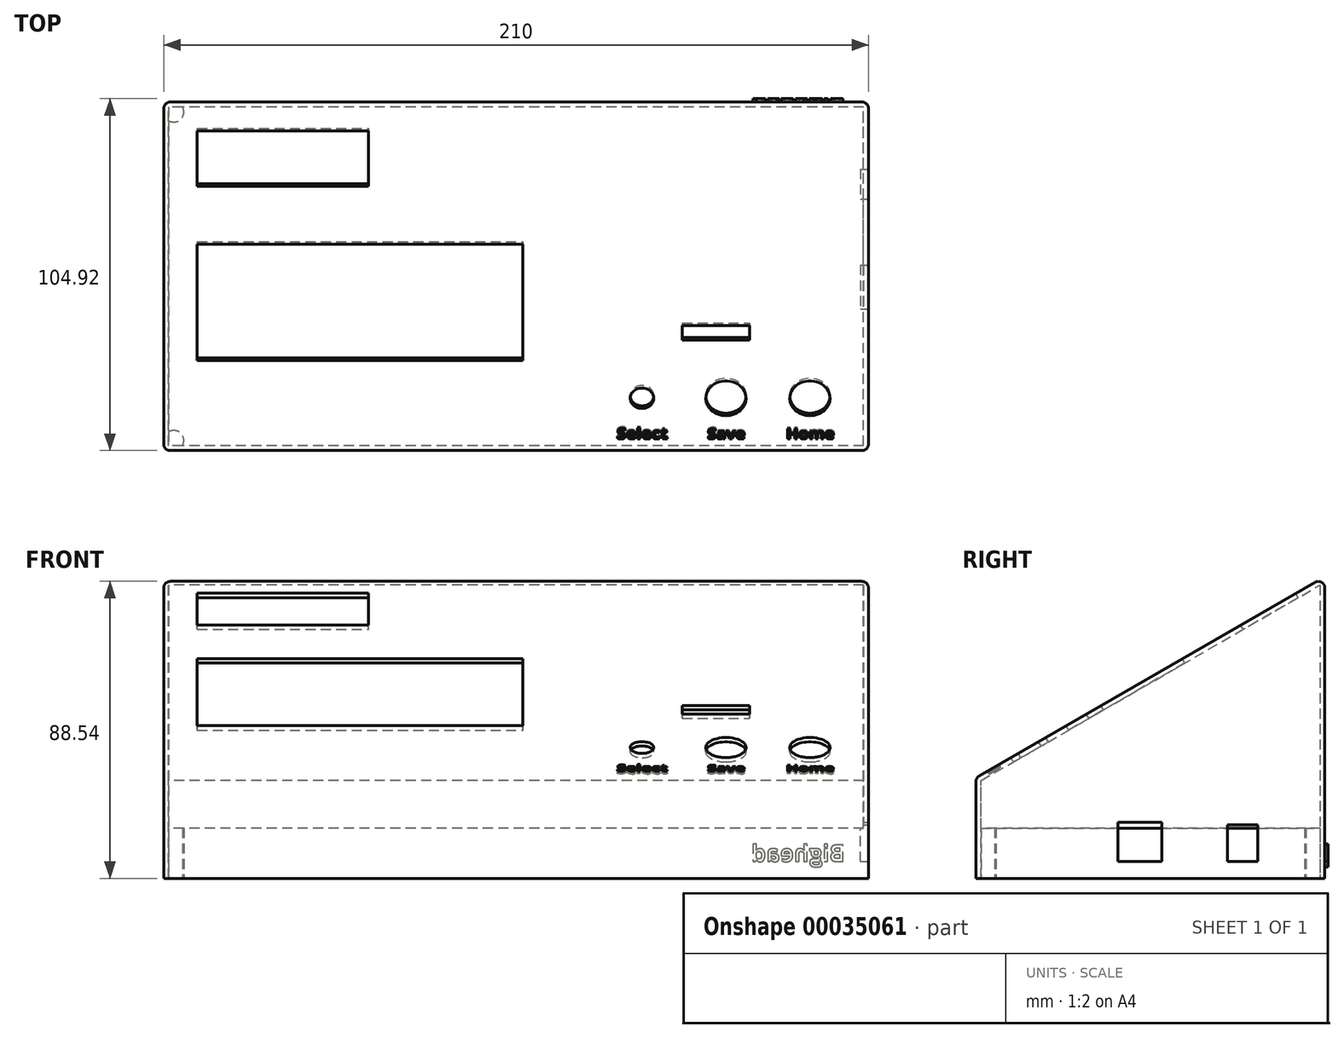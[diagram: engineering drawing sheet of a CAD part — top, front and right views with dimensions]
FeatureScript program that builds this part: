
annotation { "Feature Type Name" : "Feature", "Feature Type Description" : "" }
export const myFeature = defineFeature(function(context is Context, id is Id, definition is map)
    precondition{}
    {
        {
            var Q0;
            Q0=qCreatedBy(makeId("Right.planeOp"),FACE);
            var sketch = newSketch(context, id + "F0", { "sketchPlane" : qUnion([Q0])});
            skLineSegment(sketch, "E0", {"start": v(0, 0) * mm, "end": v(0, 30) * mm});
            skLineSegment(sketch, "E1", {"start": v(0, 30) * mm, "end": v(103.92, 90) * mm});
            skLineSegment(sketch, "E2", {"start": v(103.92, 90) * mm, "end": v(103.92, 0) * mm});
            skLineSegment(sketch, "E3", {"start": v(103.92, 0) * mm, "end": v(0, 0) * mm});
            skSolve(sketch);
        }
        {
            var Q0;
            Q0 = qSketchRegion(id + "F0", true);
            extrude(context, id + "F1", {"entities" : qUnion([Q0]), "depth" : 210 * mm});
        }
        {
            var Q0;
            Q0=makeQuery(id+"F1.opExtrude","SWEPT_FACE",FACE,{"disambiguationData":[OSD([sQuery(id+"F0.wireOp",EDGE,"E3")])]});
            shell(context, id + "F2", {"entities" : qUnion([Q0]), "thickness" : 1.5 * mm});
        }
        {
            var Q0;
            Q0=makeQuery(id+"F1.opExtrude","SWEPT_FACE",FACE,{"disambiguationData":[OSD([sQuery(id+"F0.wireOp",EDGE,"E1")])]});
            var sketch = newSketch(context, id + "F3", { "sketchPlane" : qUnion([Q0])});
            skLineSegment(sketch, "E4.bottom", {"start": v(10, 125) * mm, "end": v(61, 125) * mm});
            skLineSegment(sketch, "E4.top", {"start": v(10, 106) * mm, "end": v(61, 106) * mm});
            skLineSegment(sketch, "E4.left", {"start": v(10, 125) * mm, "end": v(10, 106) * mm});
            skLineSegment(sketch, "E4.right", {"start": v(61, 125) * mm, "end": v(61, 106) * mm});
            skLineSegment(sketch, "E5.bottom", {"start": v(10, 86) * mm, "end": v(107, 86) * mm});
            skLineSegment(sketch, "E5.top", {"start": v(10, 46) * mm, "end": v(107, 46) * mm});
            skLineSegment(sketch, "E5.left", {"start": v(10, 86) * mm, "end": v(10, 46) * mm});
            skLineSegment(sketch, "E5.right", {"start": v(107, 86) * mm, "end": v(107, 46) * mm});
            skCircle(sketch, "E6", {"center": v(142.5, 33) * mm, "radius": 3.5 * mm});
            skCircle(sketch, "E7", {"center": v(167.5, 33) * mm, "radius": 6 * mm});
            skCircle(sketch, "E8", {"center": v(192.5, 33) * mm, "radius": 6 * mm});
            skCircle(sketch, "E9", {"center": v(192.5, 33) * mm, "radius": 8.75 * mm, "construction": true});
            skSolve(sketch);
        }
        {
            var Q0;
            Q0 = qSketchRegion(id + "F3", true);
            extrude(context, id + "F4", {"entities" : qUnion([Q0]), "operationType" : NewBodyOperationType.REMOVE, "oppositeDirection" : true, "depth" : 2.5 * mm});
        }
        {
            var Q0;
            Q0=makeQuery(id+"F3.imprint","IMPRINT",FACE,{"disambiguationData":[TD([[makeQuery(id+"F3.imprint","IMPRINT",EDGE,{"derivedFrom":sQuery(id+"F3.wireOp",EDGE,"E4.bottom")}),1.0]])]});
            var sketch = newSketch(context, id + "F5", { "sketchPlane" : qUnion([Q0])});
            skLineSegment(sketch, "E10.bottom", {"start": v(129, 125) * mm, "end": v(200, 125) * mm, "construction": true});
            skLineSegment(sketch, "E10.top", {"start": v(129, 48) * mm, "end": v(200, 48) * mm, "construction": true});
            skLineSegment(sketch, "E10.left", {"start": v(129, 125) * mm, "end": v(129, 48) * mm, "construction": true});
            skLineSegment(sketch, "E10.right", {"start": v(200, 125) * mm, "end": v(200, 48) * mm, "construction": true});
            skLineSegment(sketch, "E11.bottom", {"start": v(154.5, 58) * mm, "end": v(174.5, 58) * mm});
            skLineSegment(sketch, "E11.top", {"start": v(154.5, 53) * mm, "end": v(174.5, 53) * mm});
            skLineSegment(sketch, "E11.left", {"start": v(154.5, 58) * mm, "end": v(154.5, 53) * mm});
            skLineSegment(sketch, "E11.right", {"start": v(174.5, 58) * mm, "end": v(174.5, 53) * mm});
            skSolve(sketch);
        }
        {
            var Q0;
            Q0=makeQuery(id+"F5.imprint","IMPRINT",FACE,{"disambiguationData":[TD([[makeQuery(id+"F5.imprint","IMPRINT",EDGE,{"derivedFrom":sQuery(id+"F5.wireOp",EDGE,"E11.bottom")}),-1.0]])]});
            extrude(context, id + "F6", {"entities" : qUnion([Q0]), "operationType" : NewBodyOperationType.REMOVE, "oppositeDirection" : true, "depth" : 2.5 * mm});
        }
        {
            var Q0;
            Q0=makeQuery(id+"F3.imprint","IMPRINT",FACE,{"disambiguationData":[TD([[makeQuery(id+"F3.imprint","IMPRINT",EDGE,{"derivedFrom":sQuery(id+"F3.wireOp",EDGE,"E4.bottom")}),1.0]])]});
            var sketch = newSketch(context, id + "F7", { "sketchPlane" : qUnion([Q0])});
            skText(sketch, "E12", { "text": "Save", "fontName": "OpenSans-Bold.ttf"});
            skText(sketch, "E13", { "text": "Home", "fontName": "OpenSans-Bold.ttf"});
            skText(sketch, "E14", { "text": "Select", "fontName": "OpenSans-Bold.ttf"});
            const initialGuessF7  = {"E12": [0.16198, 0.019, 1, 0, 0.0035], "E13": [0.18542, 0.019, 1, 0, 0.0035], "E14": [0.13498, 0.019, 1, 0, 0.00366]};
            skSetInitialGuess(sketch, initialGuessF7);
            skSolve(sketch);
        }
        {
            var Q0;
            Q0 = qSketchRegion(id + "F7", true);
            extrude(context, id + "F8", {"entities" : qUnion([Q0]), "operationType" : NewBodyOperationType.REMOVE, "oppositeDirection" : true, "depth" : 1 * mm});
        }
        {
            var Q0;
            Q0=makeQuery(id+"F1.opExtrude","SWEPT_EDGE",EDGE,{"disambiguationData":[OSD([sQuery(id+"F0.wireOp",EDGE,"E1"),sQuery(id+"F0.wireOp",EDGE,"E2")])]});
            var Q1;
            Q1=makeQuery(id+"F1.opExtrude","CAP_EDGE",EDGE,{"disambiguationData":[OSD([sQuery(id+"F0.wireOp",EDGE,"E1")])],"isStart":false});
            var Q2;
            Q2=makeQuery(id+"F1.opExtrude","SWEPT_EDGE",EDGE,{"disambiguationData":[OSD([sQuery(id+"F0.wireOp",EDGE,"E0"),sQuery(id+"F0.wireOp",EDGE,"E1")])]});
            var Q3;
            Q3=makeQuery(id+"F1.opExtrude","CAP_EDGE",EDGE,{"disambiguationData":[OSD([sQuery(id+"F0.wireOp",EDGE,"E0")])],"isStart":false});
            var Q4;
            Q4=makeQuery(id+"F1.opExtrude","CAP_EDGE",EDGE,{"disambiguationData":[OSD([sQuery(id+"F0.wireOp",EDGE,"E1")])],"isStart":true});
            var Q5;
            Q5=makeQuery(id+"F1.opExtrude","CAP_EDGE",EDGE,{"disambiguationData":[OSD([sQuery(id+"F0.wireOp",EDGE,"E2")])],"isStart":true});
            var Q6;
            Q6=makeQuery(id+"F1.opExtrude","CAP_EDGE",EDGE,{"disambiguationData":[OSD([sQuery(id+"F0.wireOp",EDGE,"E0")])],"isStart":true});
            var Q7;
            Q7=makeQuery(id+"F1.opExtrude","CAP_EDGE",EDGE,{"disambiguationData":[OSD([sQuery(id+"F0.wireOp",EDGE,"E2")])],"isStart":false});
            fillet(context, id + "F9", {"entities" : qUnion([Q0, Q1, Q2, Q3, Q4, Q5, Q6, Q7]), "radius" : (2) * mm, "tangentPropagation" : true, "allowEdgeOverflow" : false});
        }
        {
            var Q0;
            Q0=makeQuery(id+"F1.opExtrude","SWEPT_FACE",FACE,{"disambiguationData":[OSD([sQuery(id+"F0.wireOp",EDGE,"E3")])]});
            var sketch = newSketch(context, id + "F10", { "sketchPlane" : qUnion([Q0])});
            skCircle(sketch, "E15", {"center": v(206, -99.92) * mm, "radius": 3 * mm});
            skCircle(sketch, "E16", {"center": v(206, -99.92) * mm, "radius": 2 * mm, "construction": true});
            skSolve(sketch);
        }
        {
            var Q0;
            Q0 = qSketchRegion(id + "F10", true);
            extrude(context, id + "F11", {"entities" : qUnion([Q0]), "operationType" : NewBodyOperationType.ADD, "oppositeDirection" : true, "depth" : 15 * mm});
        }
        {
            var Q0;
            {var subQ0=sQuery(id+"F0.wireOp",EDGE,"E3");var subQ10=makeQuery(id+"F1.opExtrude","CAP_EDGE",EDGE,{"disambiguationData":[OSD([subQ0])],"isStart":true});Q0=makeQuery(id+"F10.imprint","IMPRINT",FACE,{"disambiguationData":[TD([[makeQuery(id+"F10.imprint","IMPRINT",EDGE,{"derivedFrom":subQ10}),-1.0]])]});}
            var sketch = newSketch(context, id + "F12", { "sketchPlane" : qUnion([Q0])});
            skCircle(sketch, "E17", {"center": v(206, -4) * mm, "radius": 3 * mm});
            skSolve(sketch);
        }
        {
            var Q0;
            {var subQ0=sQuery(id+"F0.wireOp",EDGE,"E3");var subQ2=makeQuery(id+"F2.opShell","OFFSET_EDGE",EDGE,{"disambiguationData":[OSD([sQuery(id+"F0.wireOp",EDGE,"E0"),subQ0])]});var subQ4=sQuery(id+"F12.wireOp",EDGE,"E17");var subQ6=makeQuery(id+"F10.imprint","IMPRINT",EDGE,{"derivedFrom":subQ2});var subQ8=makeQuery(id+"F12.imprint","INTERSECT",VERTEX,{"derivedFrom":[subQ6,subQ4]});Q0=makeQuery(id+"F12.imprint","IMPRINT",FACE,{"disambiguationData":[TD([[makeQuery(id+"F12.imprint","IMPRINT",EDGE,{"disambiguationData":[TD([[subQ8,-1.0]])],"derivedFrom":subQ4}),1.0]])]});}
            var Q1;
            {var subQ0=sQuery(id+"F0.wireOp",EDGE,"E3");var subQ2=makeQuery(id+"F2.opShell","OFFSET_EDGE",EDGE,{"disambiguationData":[OSD([sQuery(id+"F0.wireOp",EDGE,"E0"),subQ0])]});var subQ4=sQuery(id+"F12.wireOp",EDGE,"E17");var subQ6=makeQuery(id+"F10.imprint","IMPRINT",EDGE,{"derivedFrom":subQ2});var subQ8=makeQuery(id+"F12.imprint","INTERSECT",VERTEX,{"derivedFrom":[subQ6,subQ4]});Q1=makeQuery(id+"F12.imprint","IMPRINT",FACE,{"disambiguationData":[TD([[makeQuery(id+"F12.imprint","IMPRINT",EDGE,{"disambiguationData":[TD([[subQ8,1.0]])],"derivedFrom":subQ4}),1.0]])]});}
            extrude(context, id + "F13", {"entities" : qUnion([Q0, Q1]), "operationType" : NewBodyOperationType.ADD, "oppositeDirection" : true, "depth" : 15 * mm});
        }
        {
            var Q0;
            {var subQ0=sQuery(id+"F0.wireOp",EDGE,"E3");var subQ10=makeQuery(id+"F1.opExtrude","CAP_EDGE",EDGE,{"disambiguationData":[OSD([subQ0])],"isStart":true});Q0=makeQuery(id+"F10.imprint","IMPRINT",FACE,{"disambiguationData":[TD([[makeQuery(id+"F10.imprint","IMPRINT",EDGE,{"derivedFrom":subQ10}),-1.0]])]});}
            var sketch = newSketch(context, id + "F14", { "sketchPlane" : qUnion([Q0])});
            skCircle(sketch, "E18", {"center": v(3, -100.92) * mm, "radius": 3 * mm});
            skCircle(sketch, "E19", {"center": v(3, -3) * mm, "radius": 3 * mm});
            skSolve(sketch);
        }
        {
            var Q0;
            {var subQ0=sQuery(id+"F0.wireOp",EDGE,"E3");var subQ2=sQuery(id+"F14.wireOp",EDGE,"E19");var subQ5=makeQuery(id+"F10.imprint","IMPRINT",EDGE,{"derivedFrom":makeQuery(id+"F2.opShell","OFFSET_EDGE",EDGE,{"disambiguationData":[OSD([subQ0]),TDD([makeQuery(id+"F1.opExtrude","CAP_EDGE",EDGE,{"disambiguationData":[OSD([subQ0])],"isStart":true})])]})});var subQ7=makeQuery(id+"F14.imprint","INTERSECT",VERTEX,{"disambiguationData":[OD(0.0)],"derivedFrom":[subQ5,subQ2]});Q0=makeQuery(id+"F14.imprint","IMPRINT",FACE,{"disambiguationData":[TD([[makeQuery(id+"F14.imprint","IMPRINT",EDGE,{"disambiguationData":[TD([[subQ7,1.0]])],"derivedFrom":subQ5}),-1.0]])]});}
            var Q1;
            {var subQ0=sQuery(id+"F0.wireOp",EDGE,"E3");var subQ2=makeQuery(id+"F2.opShell","OFFSET_EDGE",EDGE,{"disambiguationData":[OSD([subQ0]),TDD([makeQuery(id+"F1.opExtrude","CAP_EDGE",EDGE,{"disambiguationData":[OSD([subQ0])],"isStart":true})])]});var subQ4=sQuery(id+"F14.wireOp",EDGE,"E18");var subQ7=makeQuery(id+"F10.imprint","IMPRINT",EDGE,{"derivedFrom":subQ2});var subQ9=makeQuery(id+"F14.imprint","INTERSECT",VERTEX,{"disambiguationData":[OD(0.0)],"derivedFrom":[subQ7,subQ4]});Q1=makeQuery(id+"F14.imprint","IMPRINT",FACE,{"disambiguationData":[TD([[makeQuery(id+"F14.imprint","IMPRINT",EDGE,{"disambiguationData":[TD([[subQ9,-1.0]])],"derivedFrom":subQ7}),-1.0]])]});}
            extrude(context, id + "F15", {"entities" : qUnion([Q0, Q1]), "operationType" : NewBodyOperationType.ADD, "oppositeDirection" : true, "depth" : 15 * mm});
        }
        {
            var Q0;
            Q0=makeQuery(id+"F1.opExtrude","CAP_FACE",FACE,{"disambiguationData":[OSD([sQuery(id+"F0.wireOp",EDGE,"E0"),sQuery(id+"F0.wireOp",EDGE,"E1"),sQuery(id+"F0.wireOp",EDGE,"E2"),sQuery(id+"F0.wireOp",EDGE,"E3")])],"isStart":false});
            var sketch = newSketch(context, id + "F16", { "sketchPlane" : qUnion([Q0])});
            skLineSegment(sketch, "E20.bottom", {"start": v(74.92, 5) * mm, "end": v(83.92, 5) * mm});
            skLineSegment(sketch, "E20.top", {"start": v(74.92, 16) * mm, "end": v(83.92, 16) * mm});
            skLineSegment(sketch, "E20.left", {"start": v(74.92, 5) * mm, "end": v(74.92, 16) * mm});
            skLineSegment(sketch, "E20.right", {"start": v(83.92, 5) * mm, "end": v(83.92, 16) * mm});
            skLineSegment(sketch, "E21.bottom", {"start": v(55.32, 5) * mm, "end": v(42.22, 5) * mm});
            skLineSegment(sketch, "E21.top", {"start": v(55.32, 16.7) * mm, "end": v(42.22, 16.7) * mm});
            skLineSegment(sketch, "E21.left", {"start": v(55.32, 5) * mm, "end": v(55.32, 16.7) * mm});
            skLineSegment(sketch, "E21.right", {"start": v(42.22, 5) * mm, "end": v(42.22, 16.7) * mm});
            skSolve(sketch);
        }
        {
            var Q0;
            Q0=makeQuery(id+"F16.imprint","IMPRINT",FACE,{"disambiguationData":[TD([[makeQuery(id+"F16.imprint","IMPRINT",EDGE,{"derivedFrom":sQuery(id+"F16.wireOp",EDGE,"E20.bottom")}),1.0]])]});
            var Q1;
            Q1=makeQuery(id+"F16.imprint","IMPRINT",FACE,{"disambiguationData":[TD([[makeQuery(id+"F16.imprint","IMPRINT",EDGE,{"derivedFrom":sQuery(id+"F16.wireOp",EDGE,"E21.bottom")}),-1.0]])]});
            extrude(context, id + "F17", {"entities" : qUnion([Q0, Q1]), "operationType" : NewBodyOperationType.REMOVE, "oppositeDirection" : true, "depth" : 2.5 * mm});
        }
        {
            var Q0;
            Q0=makeQuery(id+"F1.opExtrude","SWEPT_FACE",FACE,{"disambiguationData":[OSD([sQuery(id+"F0.wireOp",EDGE,"E2")])]});
            var sketch = newSketch(context, id + "F18", { "sketchPlane" : qUnion([Q0])});
            skText(sketch, "E22", { "text": "Bighead", "fontName": "OpenSans-Bold.ttf"});
            const initialGuessF18  = {"E22": [-0.203, 0.005, 1, 0, 0.005]};
            skSetInitialGuess(sketch, initialGuessF18);
            skSolve(sketch);
        }
        {
            var Q0;
            Q0 = qSketchRegion(id + "F18", true);
            extrude(context, id + "F19", {"entities" : qUnion([Q0]), "operationType" : NewBodyOperationType.ADD, "depth" : 1 * mm});
        }
    });
